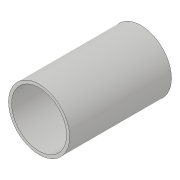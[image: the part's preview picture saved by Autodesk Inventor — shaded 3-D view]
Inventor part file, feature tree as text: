
AUTODESK INVENTOR PART (.ipt)
format: ipt  version: 2019 (Build 230136000, 136)  size: 85,504 bytes
history: native  units: in
note: dims shown in document units (in); Inventor stores cm internally (conversion verified against a paired STEP export)
features: extrude x2, sketch x2
ambient origin geometry x8: Origin, YZ Plane, XZ Plane, XY Plane, X Axis, Y Axis, Z Axis, Center Point
bodies: Solid1 (feature_tree)
feature tree (4):
  extrude  "Extrusion1"  Depth=1.9685in TaperAngle=0.0deg
  extrude  "Extrusion2"  Depth=1.9685in TaperAngle=0.0deg
  sketch  "Sketch1"  dims[d0=1.1811in d1=1.9685in d2=0.0in]
  sketch  "Sketch2"  dims[d3=1.063in d4=1.9685in d5=0.0in]
